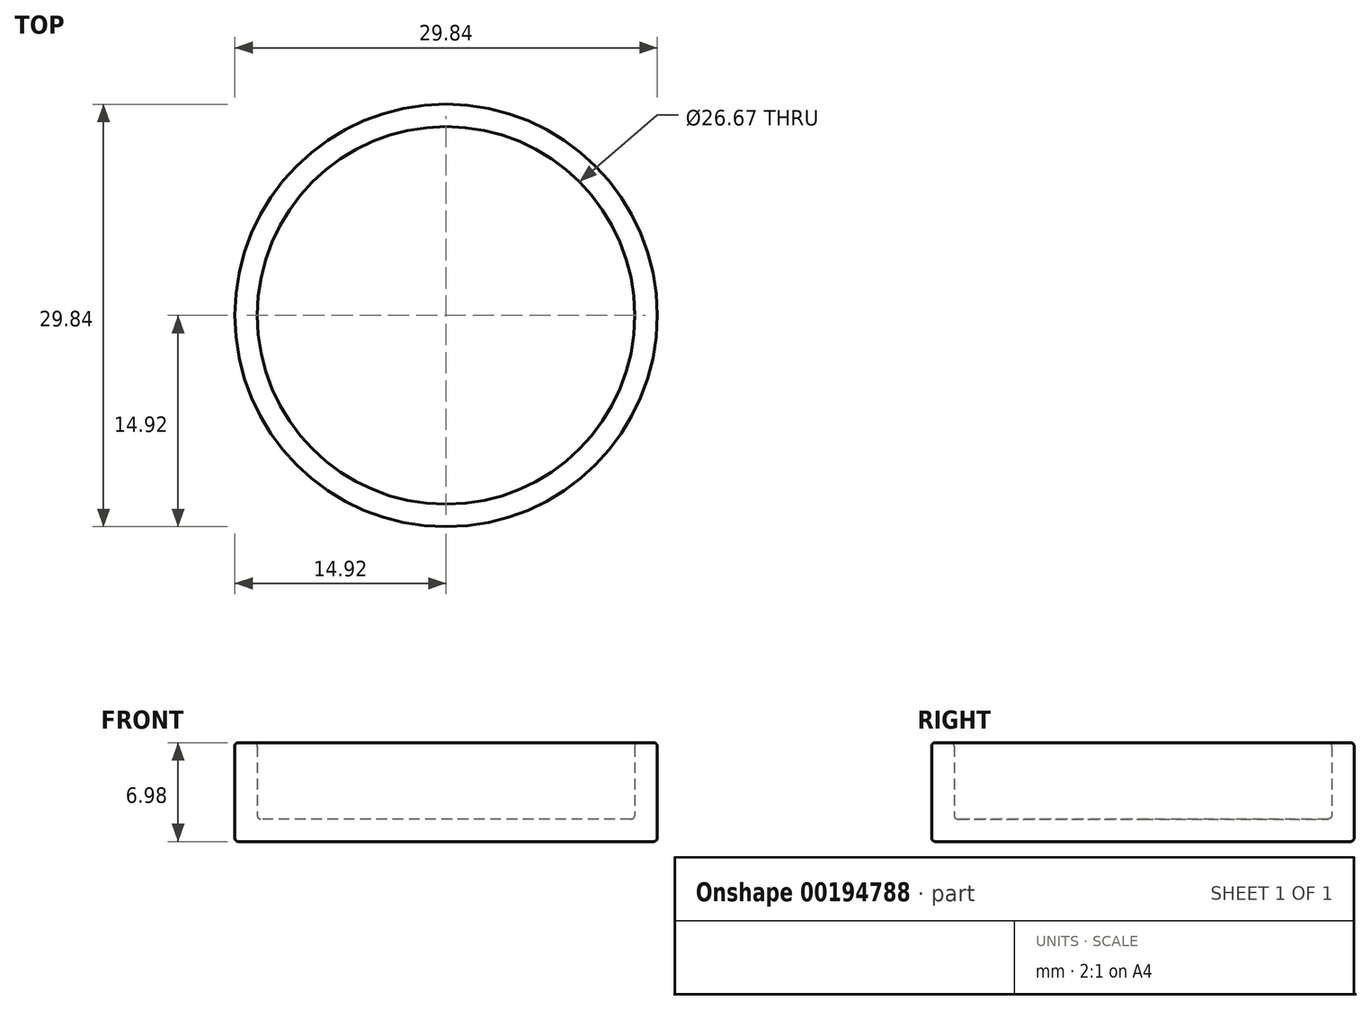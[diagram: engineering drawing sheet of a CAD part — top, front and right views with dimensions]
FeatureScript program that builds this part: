
annotation { "Feature Type Name" : "Feature", "Feature Type Description" : "" }
export const myFeature = defineFeature(function(context is Context, id is Id, definition is map)
    precondition{}
    {
        {
            var Q0;
            Q0=qCreatedBy(makeId("Top.planeOp"),FACE);
            var sketch = newSketch(context, id + "F0", { "sketchPlane" : qUnion([Q0])});
            skCircle(sketch, "E0", {"center": v(0, 0) * mm, "radius": 14.92 * mm});
            skSolve(sketch);
        }
        {
            var Q0;
            Q0=makeQuery(id+"F0.imprint","IMPRINT",FACE,{"disambiguationData":[TD([[makeQuery(id+"F0.imprint","IMPRINT",EDGE,{"derivedFrom":sQuery(id+"F0.wireOp",EDGE,"E0")}),1.0]])]});
            extrude(context, id + "F1", {"entities" : qUnion([Q0]), "endBound" : BoundingType.SYMMETRIC, "depth" : 7 * mm});
        }
        {
            var Q0;
            Q0=makeQuery(id+"F1.opExtrude","CAP_FACE",FACE,{"disambiguationData":[OSD([sQuery(id+"F0.wireOp",EDGE,"E0")])],"isStart":false});
            shell(context, id + "F2", {"entities" : qUnion([Q0]), "thickness" : 1.59 * mm});
        }
        {
            var Q0;
            {var subQ0=sQuery(id+"F0.wireOp",EDGE,"E0");Q0=makeQuery(id+"F2.opShell","OFFSET_EDGE",EDGE,{"disambiguationData":[OSD([subQ0]),TDD([makeQuery(id+"F1.opExtrude","CAP_EDGE",EDGE,{"disambiguationData":[OSD([subQ0])],"isStart":true})])]});}
            var Q1;
            {var subQ0=sQuery(id+"F0.wireOp",EDGE,"E0");Q1=makeQuery(id+"F2.opShell","OFFSET_EDGE",EDGE,{"disambiguationData":[OSD([subQ0]),TDD([makeQuery(id+"F1.opExtrude","CAP_EDGE",EDGE,{"disambiguationData":[OSD([subQ0])],"isStart":false})])]});}
            var Q2;
            Q2=makeQuery(id+"F1.opExtrude","CAP_EDGE",EDGE,{"disambiguationData":[OSD([sQuery(id+"F0.wireOp",EDGE,"E0")])],"isStart":false});
            var Q3;
            Q3=makeQuery(id+"F1.opExtrude","CAP_EDGE",EDGE,{"disambiguationData":[OSD([sQuery(id+"F0.wireOp",EDGE,"E0")])],"isStart":true});
            fillet(context, id + "F3", {"entities" : qUnion([Q0, Q1, Q2, Q3]), "radius" : 0.25 * mm, "tangentPropagation" : true, "allowEdgeOverflow" : false});
        }
    });
